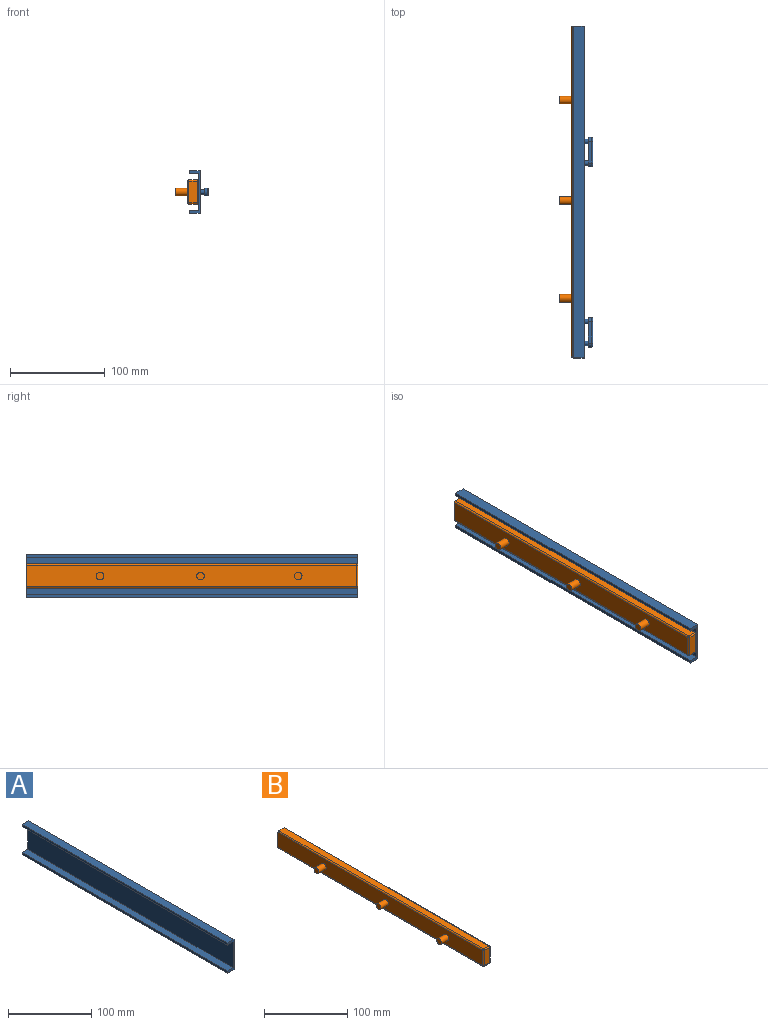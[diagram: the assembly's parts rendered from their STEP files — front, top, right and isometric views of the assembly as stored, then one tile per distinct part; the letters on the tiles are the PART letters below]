
ASSEMBLY  parts=2 mates=1
PART A: 34 faces, bbox 20.1x350x44.5 mm
  f0: plane 350x3.18mm, normal (-1,0,0), area 1111.2mm2, adj f1,f2,f3,f7
  f1: plane 44.45x11.11mm, normal (0,-1,0), area 130.1mm2, adj f0,f2,f4,f5,f6,f7,f8,f9
  f2: plane 350x11.11mm, normal (0,0,-1), area 3889.4mm2, adj f0,f1,f3,f6
  f3: plane 44.45x11.11mm, normal (0,1,0), area 130.1mm2, adj f0,f2,f4,f5,f6,f7,f8,f9
  f4: plane 350x11.11mm, normal (0,0,1), area 3889.4mm2, adj f1,f3,f5,f6
  f5: plane 350x3.18mm, normal (-1,0,0), area 1111.3mm2, adj f1,f3,f4,f8
  f6: plane 350x44.45mm, normal (1,0,0), area 15486.6mm2, adj f1,f2,f3,f4,f10,f11,f12,f13
  f7: plane 350x9.55mm, normal (0,0,1), area 3342.6mm2, adj f0,f1,f3,f9
  f8: plane 350x9.55mm, normal (0,0,-1), area 3342.6mm2, adj f1,f3,f5,f9
  f9: plane 350x38.1mm, normal (-1,0,0), area 13335mm2, adj f1,f3,f7,f8
  f10: cylinder r=2.37mm len=4.75mm, axis (-1,0,0), area 67.1mm2, adj f6,f19
  f11: cylinder r=2.37mm len=4.75mm, axis (-1,0,0), area 67.1mm2, adj f6,f19
  f12: cylinder r=2.37mm len=4.75mm, axis (-1,0,0), area 67.1mm2, adj f6,f25
  f13: cylinder r=2.37mm len=4.75mm, axis (-1,0,0), area 67.1mm2, adj f6,f25
  f14: cylinder r=4mm len=8mm, axis (-1,0,0), area 43.8mm2, adj f15,f17,f19,f31
  f15: plane 23x3.48mm, normal (0,0,-1), area 80.1mm2, adj f14,f16,f19,f30
  f16: cylinder r=4mm len=8mm, axis (-1,0,0), area 43.8mm2, adj f15,f17,f19,f32
  f17: plane 23x3.48mm, normal (0,0,1), area 80.1mm2, adj f14,f16,f19,f33
  f18: plane 28.97x5.97mm, normal (1,0,0), area 165.2mm2, adj f30,f31,f32,f33
  f19: plane 31x8mm, normal (-1,0,0), area 198.8mm2, adj f10,f11,f14,f15,f16,f17
  f20: plane 23x3.48mm, normal (0,0,1), area 80.1mm2, adj f21,f23,f25,f29
  f21: cylinder r=4mm len=8mm, axis (-1,0,0), area 43.8mm2, adj f20,f22,f25,f27
  f22: plane 23x3.48mm, normal (0,0,-1), area 80.1mm2, adj f21,f23,f25,f26
  f23: cylinder r=4mm len=8mm, axis (-1,0,0), area 43.8mm2, adj f20,f22,f25,f28
  f24: plane 28.97x5.97mm, normal (1,0,0), area 165.2mm2, adj f26,f27,f28,f29
  f25: plane 31x8mm, normal (-1,0,0), area 198.8mm2, adj f12,f13,f20,f21,f22,f23
  f26: cylinder r=1.02mm len=23mm, axis (0,1,0), area 36.7mm2, adj f22,f24,f27,f28
  f27: torus R=2.98mm, axis (1,0,0), area 18.2mm2, adj f21,f24,f26,f29
  f28: torus R=2.98mm, axis (1,0,0), area 18.2mm2, adj f23,f24,f26,f29
  f29: cylinder r=1.02mm len=23mm, axis (0,-1,0), area 36.7mm2, adj f20,f24,f27,f28
  f30: cylinder r=1.02mm len=23mm, axis (0,1,0), area 36.7mm2, adj f15,f18,f31,f32
  f31: torus R=2.98mm, axis (1,0,0), area 18.2mm2, adj f14,f18,f30,f33
  f32: torus R=2.98mm, axis (1,0,0), area 18.2mm2, adj f16,f18,f30,f33
  f33: cylinder r=1.02mm len=23mm, axis (0,-1,0), area 36.7mm2, adj f17,f18,f31,f32
PART B: 24 faces, bbox 24.6x350x25.4 mm
  f0: plane 348.43x8.76mm, normal (0,0,-1), area 3053.3mm2, adj f1,f12,f13,f14
  f1: plane 25.4x11.91mm, normal (0,1,0), area 300.5mm2, adj f0,f2,f4,f5,f12,f14,f17,f20
  f2: plane 348.43x8.76mm, normal (0,0,1), area 3053.3mm2, adj f1,f17,f20,f23
  f3: plane 22.25x8.76mm, normal (0,-1,0), area 195mm2, adj f13,f18,f19,f23
  f4: plane 348.43x22.25mm, normal (-1,0,0), area 7601.8mm2, adj f1,f6,f8,f10,f12,f17,f18
  f5: plane 348.43x22.25mm, normal (1,0,0), area 7752.6mm2, adj f1,f14,f19,f20
  f6: cylinder r=4mm len=12.7mm, axis (1,0,0), area 319.2mm2, adj f4,f7
  f7: plane 8x8mm, normal (-1,0,0), area 50.3mm2, adj f6
  f8: cylinder r=4mm len=12.7mm, axis (1,0,0), area 319.2mm2, adj f4,f9
  f9: plane 8x8mm, normal (-1,0,0), area 50.3mm2, adj f8
  f10: cylinder r=4mm len=12.7mm, axis (1,0,0), area 319.2mm2, adj f4,f11
  f11: plane 8x8mm, normal (-1,0,0), area 50.3mm2, adj f10
  f12: cylinder r=1.57mm len=348.43mm, axis (0,-1,0), area 861.9mm2, adj f0,f1,f4,f15
  f13: cylinder r=1.57mm len=8.76mm, axis (1,0,0), area 21.7mm2, adj f0,f3,f15,f16
  f14: cylinder r=1.57mm len=348.43mm, axis (0,1,0), area 861.9mm2, adj f0,f1,f5,f16
  f15: sphere r=1.57mm, area 3.9mm2, adj f12,f13,f18
  f16: sphere r=1.57mm, area 3.9mm2, adj f13,f14,f19
  f17: cylinder r=1.57mm len=348.43mm, axis (0,1,0), area 861.9mm2, adj f1,f2,f4,f21
  f18: cylinder r=1.57mm len=22.25mm, axis (0,0,1), area 55mm2, adj f3,f4,f15,f21
  f19: cylinder r=1.57mm len=22.25mm, axis (0,0,-1), area 55mm2, adj f3,f5,f16,f22
  f20: cylinder r=1.57mm len=348.43mm, axis (0,-1,0), area 861.9mm2, adj f1,f2,f5,f22
  f21: sphere r=1.57mm, area 3.9mm2, adj f17,f18,f23
  f22: sphere r=1.57mm, area 3.9mm2, adj f19,f20,f23
  f23: cylinder r=1.57mm len=8.76mm, axis (-1,0,0), area 21.7mm2, adj f2,f3,f21,f22
PLACE A t=(28.27,7.48,-15.11)mm fixed
PLACE B t=(6.01,7.48,-15.11)mm
MATE fastened B.f5 <-> A.f9  axis (1,0,0) through (29.84,169.78,-15.11)mm
